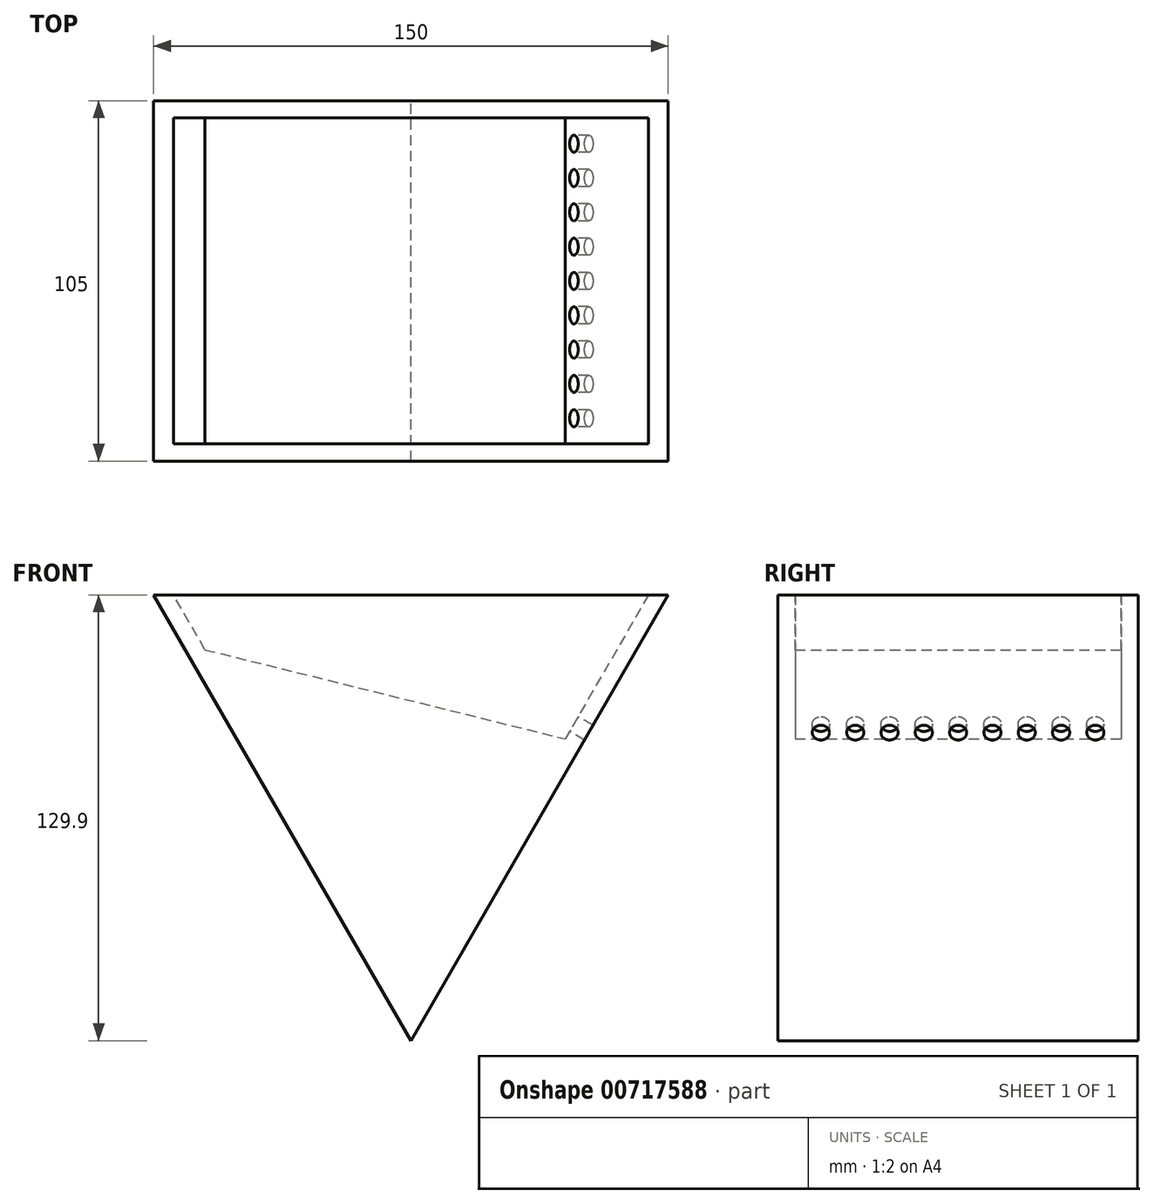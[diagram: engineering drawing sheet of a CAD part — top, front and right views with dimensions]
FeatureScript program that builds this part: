
annotation { "Feature Type Name" : "Feature", "Feature Type Description" : "" }
export const myFeature = defineFeature(function(context is Context, id is Id, definition is map)
    precondition{}
    {
        {
            var Q0;
            Q0=qCreatedBy(makeId("Front.planeOp"),FACE);
            var sketch = newSketch(context, id + "F0", { "sketchPlane" : qUnion([Q0])});
            skLineSegment(sketch, "E0", {"start": v(-75.43, 75.52) * mm, "end": v(74.57, 75.52) * mm});
            skLineSegment(sketch, "E1", {"start": v(74.57, 75.52) * mm, "end": v(-0.43, -54.38) * mm});
            skLineSegment(sketch, "E2", {"start": v(-0.43, -54.38) * mm, "end": v(-75.43, 75.52) * mm});
            skSolve(sketch);
        }
        {
            var Q0;
            Q0=makeQuery(id+"F0.imprint","IMPRINT",FACE,{"disambiguationData":[TD([[makeQuery(id+"F0.imprint","IMPRINT",EDGE,{"derivedFrom":sQuery(id+"F0.wireOp",EDGE,"E0")}),-1.0]])]});
            extrude(context, id + "F1", {"entities" : qUnion([Q0]), "depth" : 105 * mm});
        }
        {
            var Q0;
            Q0=makeQuery(id+"F1.opExtrude","SWEPT_FACE",FACE,{"disambiguationData":[OSD([sQuery(id+"F0.wireOp",EDGE,"E0")])]});
            shell(context, id + "F2", {"entities" : qUnion([Q0]), "thickness" : 5 * mm});
        }
        {
            var Q0;
            {var subQ0=sQuery(id+"F0.wireOp",EDGE,"E2");var subQ1=sQuery(id+"F0.wireOp",EDGE,"E1");var subQ2=sQuery(id+"F0.wireOp",EDGE,"E0");Q0=makeQuery(id+"F2.opShell","OFFSET_FACE",FACE,{"disambiguationData":[OSD([subQ2,subQ1,subQ0]),TDD([makeQuery(id+"F1.opExtrude","CAP_FACE",FACE,{"disambiguationData":[OSD([subQ2,subQ1,subQ0])],"isStart":true})])]});}
            var sketch = newSketch(context, id + "F3", { "sketchPlane" : qUnion([Q0])});
            skLineSegment(sketch, "E3", {"start": v(-60.43, 59.54) * mm, "end": v(44.57, 33.56) * mm});
            skLineSegment(sketch, "E4", {"start": v(44.57, 33.56) * mm, "end": v(-0.43, -44.38) * mm});
            skLineSegment(sketch, "E5", {"start": v(-0.43, -44.38) * mm, "end": v(-60.43, 59.54) * mm});
            skSolve(sketch);
        }
        {
            var Q0;
            Q0=makeQuery(id+"F3.imprint","IMPRINT",FACE,{"disambiguationData":[TD([[makeQuery(id+"F3.imprint","IMPRINT",EDGE,{"derivedFrom":sQuery(id+"F3.wireOp",EDGE,"E3")}),-1.0]])]});
            extrude(context, id + "F4", {"entities" : qUnion([Q0]), "operationType" : NewBodyOperationType.ADD, "depth" : 95 * mm});
        }
        {
            var Q0;
            Q0=makeQuery(id+"F2.opShell","OFFSET_FACE",FACE,{"disambiguationData":[OSD([sQuery(id+"F0.wireOp",EDGE,"E1")])]});
            var sketch = newSketch(context, id + "F5", { "sketchPlane" : qUnion([Q0])});
            skCircle(sketch, "E6", {"center": v(92.5, 56.35) * mm, "radius": 2.5 * mm});
            skLineSegment(sketch, "E7", {"start": v(100, 51.35) * mm, "end": v(5, 51.35) * mm});
            skLineSegment(sketch, "E8.0", {"start": v(100, 56.35) * mm, "end": v(5, 56.35) * mm});
            skCircle(sketch, "E9", {"center": v(82.5, 56.35) * mm, "radius": 2.5 * mm});
            skCircle(sketch, "E10", {"center": v(72.5, 56.35) * mm, "radius": 2.5 * mm});
            skCircle(sketch, "E11", {"center": v(62.5, 56.35) * mm, "radius": 2.5 * mm});
            skCircle(sketch, "E12", {"center": v(52.5, 56.35) * mm, "radius": 2.5 * mm});
            skCircle(sketch, "E13", {"center": v(42.5, 56.35) * mm, "radius": 2.5 * mm});
            skCircle(sketch, "E14", {"center": v(32.5, 56.35) * mm, "radius": 2.5 * mm});
            skCircle(sketch, "E15", {"center": v(22.5, 56.35) * mm, "radius": 2.5 * mm});
            skCircle(sketch, "E16", {"center": v(12.5, 56.35) * mm, "radius": 2.5 * mm});
            skSolve(sketch);
        }
        {
            var Q0;
            Q0=sQuery(id+"F5.wireOp",VERTEX,"E6.center");
            var Q1;
            Q1=sQuery(id+"F5.wireOp",VERTEX,"E9.center");
            var Q2;
            Q2=sQuery(id+"F5.wireOp",VERTEX,"E10.center");
            var Q3;
            Q3=sQuery(id+"F5.wireOp",VERTEX,"E11.center");
            var Q4;
            Q4=sQuery(id+"F5.wireOp",VERTEX,"E12.center");
            var Q5;
            Q5=sQuery(id+"F5.wireOp",VERTEX,"E13.center");
            var Q6;
            Q6=sQuery(id+"F5.wireOp",VERTEX,"E14.center");
            var Q7;
            Q7=sQuery(id+"F5.wireOp",VERTEX,"E15.center");
            var Q8;
            Q8=sQuery(id+"F5.wireOp",VERTEX,"E16.center");
            var Q9;
            Q9=makeQuery(id+"F1.opExtrude","SWEPT_BODY",BODY,{"disambiguationData":[OSD([sQuery(id+"F0.wireOp",EDGE,"E0"),sQuery(id+"F0.wireOp",EDGE,"E1"),sQuery(id+"F0.wireOp",EDGE,"E2")])]});
            hole(context, id + "F6", {"style" : HoleStyle.SIMPLE, "endStyle" : HoleEndStyle.THROUGH, "holeDiameter" : 5 * mm, "majorDiameter" : 5 * mm, "tappedDepth" : 12 * mm, "tapClearance" : 3, "locations" : qUnion([Q0, Q1, Q2, Q3, Q4, Q5, Q6, Q7, Q8]), "scope" : qUnion([Q9])});
        }
    });
